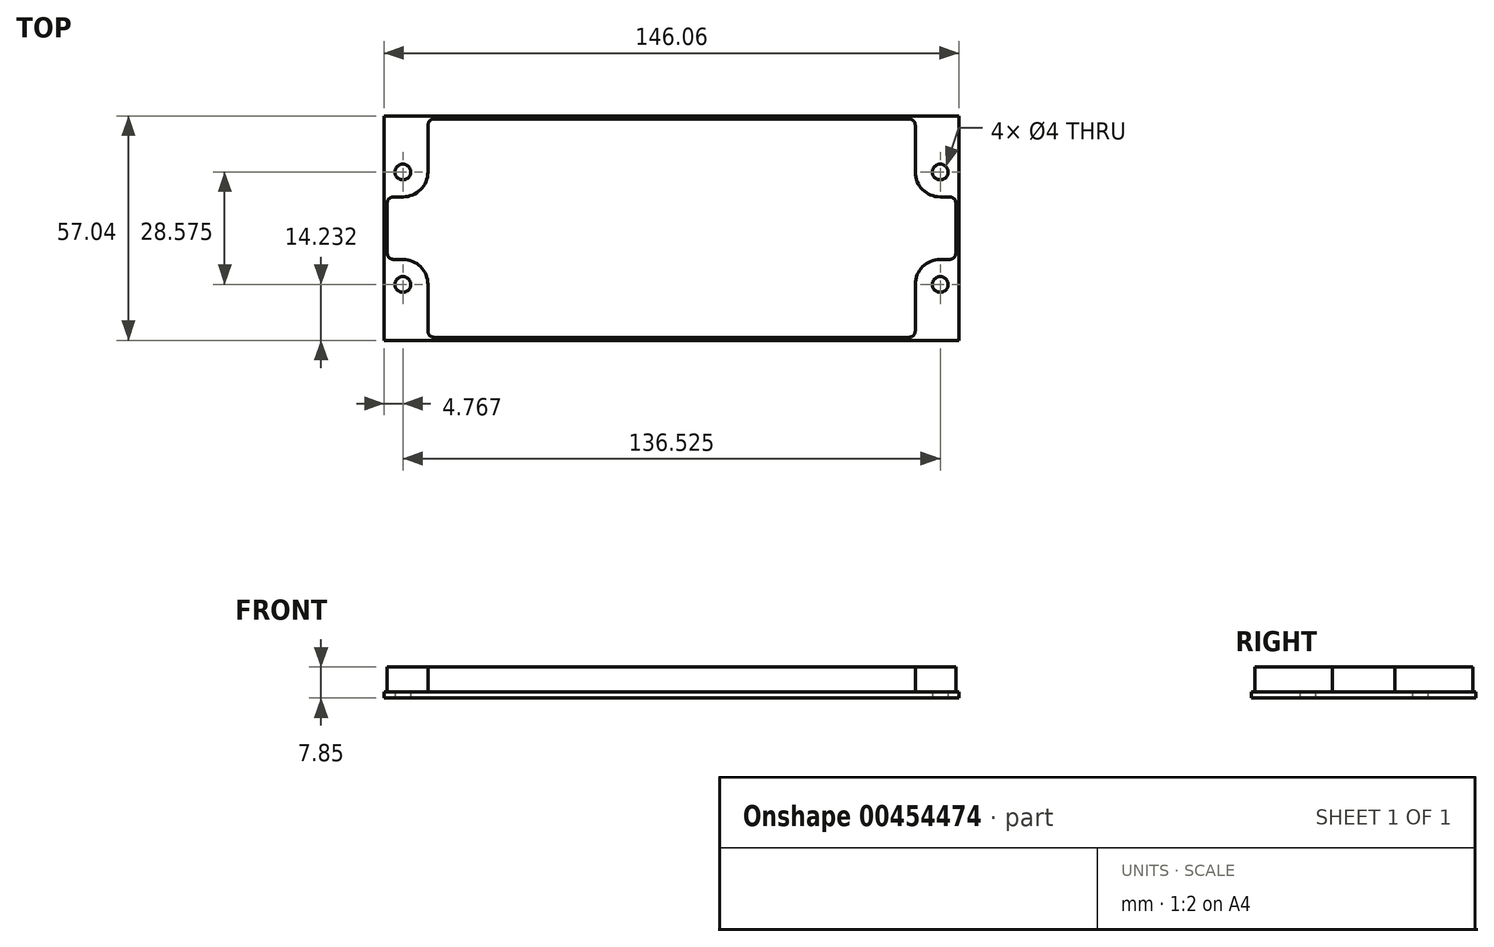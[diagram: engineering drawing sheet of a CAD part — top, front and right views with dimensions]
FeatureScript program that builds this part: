
annotation { "Feature Type Name" : "Feature", "Feature Type Description" : "" }
export const myFeature = defineFeature(function(context is Context, id is Id, definition is map)
    precondition{}
    {
        {
            var Q0;
            Q0=qCreatedBy(makeId("Top.planeOp"),FACE);
            var sketch = newSketch(context, id + "F0", { "sketchPlane" : qUnion([Q0])});
            skLineSegment(sketch, "E0.bottom", {"start": v(-73.03, 28.52) * mm, "end": v(73.03, 28.53) * mm, "construction": true});
            skLineSegment(sketch, "E0.top", {"start": v(-73.03, -28.53) * mm, "end": v(73.03, -28.52) * mm, "construction": true});
            skLineSegment(sketch, "E0.left", {"start": v(-73.03, 28.52) * mm, "end": v(-73.03, -28.53) * mm, "construction": true});
            skLineSegment(sketch, "E0.right", {"start": v(73.03, 28.53) * mm, "end": v(73.03, -28.53) * mm, "construction": true});
            skCircle(sketch, "E1", {"center": v(-68.26, -14.29) * mm, "radius": 4.76 * mm});
            skCircle(sketch, "E2", {"center": v(-68.26, 14.29) * mm, "radius": 4.76 * mm});
            skPoint(sketch, "E3.third.point.positionSnap0", {"position": v(73.03, 0) * mm});
            skCircle(sketch, "E4", {"center": v(68.26, 14.29) * mm, "radius": 4.76 * mm});
            skCircle(sketch, "E5", {"center": v(68.26, -14.29) * mm, "radius": 4.76 * mm});
            skPoint(sketch, "E6", {"position": v(0, 28.53) * mm});
            skLineSegment(sketch, "E7.bottom", {"start": v(-73.03, 28.53) * mm, "end": v(73.03, 28.53) * mm});
            skLineSegment(sketch, "E7.top", {"start": v(-73.03, -28.53) * mm, "end": v(73.03, -28.53) * mm});
            skLineSegment(sketch, "E7.left", {"start": v(-73.03, 28.52) * mm, "end": v(-73.03, -28.53) * mm});
            skLineSegment(sketch, "E7.right", {"start": v(73.03, 28.53) * mm, "end": v(73.03, -28.53) * mm});
            skCircle(sketch, "E8", {"center": v(-68.26, 14.29) * mm, "radius": 2 * mm});
            skCircle(sketch, "E9", {"center": v(68.26, -14.29) * mm, "radius": 2 * mm});
            skCircle(sketch, "E10", {"center": v(-68.26, -14.29) * mm, "radius": 2 * mm});
            skCircle(sketch, "E11", {"center": v(68.26, 14.29) * mm, "radius": 2 * mm});
            skArc(sketch, "E12", {"start": v(68.26, 20.64) * mm, "mid": v(61.91, 14.29) * mm, "end": v(68.26, 7.94) * mm});
            skArc(sketch, "E13", {"start": v(68.26, -7.94) * mm, "mid": v(61.91, -14.29) * mm, "end": v(68.26, -20.64) * mm});
            skArc(sketch, "E14", {"start": v(-68.26, -20.64) * mm, "mid": v(-61.91, -14.29) * mm, "end": v(-68.26, -7.94) * mm});
            skArc(sketch, "E15", {"start": v(-68.26, 7.94) * mm, "mid": v(-61.91, 14.29) * mm, "end": v(-68.26, 20.64) * mm});
            skLineSegment(sketch, "E16", {"start": v(68.26, 20.64) * mm, "end": v(73.03, 20.64) * mm});
            skLineSegment(sketch, "E17", {"start": v(68.26, 7.94) * mm, "end": v(73.03, 7.94) * mm});
            skLineSegment(sketch, "E18", {"start": v(68.26, -7.94) * mm, "end": v(73.03, -7.94) * mm});
            skLineSegment(sketch, "E19", {"start": v(68.26, -20.64) * mm, "end": v(73.03, -20.64) * mm});
            skLineSegment(sketch, "E20", {"start": v(-68.26, -7.94) * mm, "end": v(-73.03, -7.94) * mm});
            skLineSegment(sketch, "E21", {"start": v(-68.26, -20.64) * mm, "end": v(-73.03, -20.64) * mm});
            skLineSegment(sketch, "E22", {"start": v(-68.26, 20.64) * mm, "end": v(-73.03, 20.64) * mm});
            skLineSegment(sketch, "E23", {"start": v(-68.26, 7.94) * mm, "end": v(-73.03, 7.94) * mm});
            skSolve(sketch);
        }
        {
            var Q0;
            {var subQ3=sQuery(id+"F0.wireOp",EDGE,"E7.bottom");Q0=makeQuery(id+"F0.imprint","IMPRINT",FACE,{"disambiguationData":[TD([[makeQuery(id+"F0.imprint","IMPRINT",EDGE,{"derivedFrom":subQ3}),-1.0]])]});}
            var Q1;
            {var subQ2=sQuery(id+"F0.wireOp",EDGE,"E2");Q1=makeQuery(id+"F0.imprint","IMPRINT",FACE,{"disambiguationData":[TD([[makeQuery(id+"F0.imprint","IMPRINT",EDGE,{"derivedFrom":subQ2}),-1.0]])]});}
            var Q2;
            Q2=makeQuery(id+"F0.imprint","IMPRINT",FACE,{"disambiguationData":[TD([[makeQuery(id+"F0.imprint","IMPRINT",EDGE,{"derivedFrom":sQuery(id+"F0.wireOp",EDGE,"E2")}),1.0]])]});
            var Q3;
            {var subQ2=sQuery(id+"F0.wireOp",EDGE,"E1");Q3=makeQuery(id+"F0.imprint","IMPRINT",FACE,{"disambiguationData":[TD([[makeQuery(id+"F0.imprint","IMPRINT",EDGE,{"derivedFrom":subQ2}),-1.0]])]});}
            var Q4;
            Q4=makeQuery(id+"F0.imprint","IMPRINT",FACE,{"disambiguationData":[TD([[makeQuery(id+"F0.imprint","IMPRINT",EDGE,{"derivedFrom":sQuery(id+"F0.wireOp",EDGE,"E1")}),1.0]])]});
            var Q5;
            {var subQ2=sQuery(id+"F0.wireOp",EDGE,"E4");Q5=makeQuery(id+"F0.imprint","IMPRINT",FACE,{"disambiguationData":[TD([[makeQuery(id+"F0.imprint","IMPRINT",EDGE,{"derivedFrom":subQ2}),-1.0]])]});}
            var Q6;
            Q6=makeQuery(id+"F0.imprint","IMPRINT",FACE,{"disambiguationData":[TD([[makeQuery(id+"F0.imprint","IMPRINT",EDGE,{"derivedFrom":sQuery(id+"F0.wireOp",EDGE,"E4")}),1.0]])]});
            var Q7;
            {var subQ0=sQuery(id+"F0.wireOp",EDGE,"E5");Q7=makeQuery(id+"F0.imprint","IMPRINT",FACE,{"disambiguationData":[TD([[makeQuery(id+"F0.imprint","IMPRINT",EDGE,{"derivedFrom":subQ0}),-1.0]])]});}
            var Q8;
            Q8=makeQuery(id+"F0.imprint","IMPRINT",FACE,{"disambiguationData":[TD([[makeQuery(id+"F0.imprint","IMPRINT",EDGE,{"derivedFrom":sQuery(id+"F0.wireOp",EDGE,"E5")}),1.0]])]});
            extrude(context, id + "F1", {"entities" : qUnion([Q0, Q1, Q2, Q3, Q4, Q5, Q6, Q7, Q8]), "depth" : 1.5 * mm});
        }
        {
            var Q0;
            Q0=makeQuery(id+"F1.opExtrude","CAP_FACE",FACE,{"disambiguationData":[OSD([sQuery(id+"F0.wireOp",EDGE,"E7.bottom"),sQuery(id+"F0.wireOp",EDGE,"E7.top"),sQuery(id+"F0.wireOp",EDGE,"E7.left"),sQuery(id+"F0.wireOp",EDGE,"E7.right"),sQuery(id+"F0.wireOp",EDGE,"E8"),sQuery(id+"F0.wireOp",EDGE,"E9"),sQuery(id+"F0.wireOp",EDGE,"E10"),sQuery(id+"F0.wireOp",EDGE,"E11")])],"isStart":false});
            var sketch = newSketch(context, id + "F2", { "sketchPlane" : qUnion([Q0])});
            skLineSegment(sketch, "E24.0", {"start": v(68.26, 7.94) * mm, "end": v(70.64, 7.94) * mm});
            skArc(sketch, "E24.1", {"start": v(68.26, 20.64) * mm, "mid": v(61.91, 14.29) * mm, "end": v(68.26, 7.94) * mm});
            skLineSegment(sketch, "E24.2", {"start": v(68.26, 20.64) * mm, "end": v(70.64, 20.64) * mm});
            skLineSegment(sketch, "E25.0", {"start": v(73.03, 28.53) * mm, "end": v(73.03, -28.53) * mm});
            skLineSegment(sketch, "E25.1", {"start": v(68.26, -7.94) * mm, "end": v(70.64, -7.94) * mm});
            skArc(sketch, "E25.2", {"start": v(68.26, -7.94) * mm, "mid": v(61.91, -14.29) * mm, "end": v(68.26, -20.64) * mm});
            skLineSegment(sketch, "E25.3", {"start": v(68.26, -20.64) * mm, "end": v(70.64, -20.64) * mm});
            skLineSegment(sketch, "E25.4", {"start": v(-73.03, -28.53) * mm, "end": v(73.03, -28.53) * mm});
            skLineSegment(sketch, "E25.5", {"start": v(-73.03, 28.52) * mm, "end": v(-73.03, -28.53) * mm});
            skLineSegment(sketch, "E25.6", {"start": v(-68.26, -20.64) * mm, "end": v(-70.64, -20.64) * mm});
            skArc(sketch, "E25.7", {"start": v(-68.26, -20.64) * mm, "mid": v(-61.91, -14.29) * mm, "end": v(-68.26, -7.94) * mm});
            skLineSegment(sketch, "E25.8", {"start": v(-68.26, -7.94) * mm, "end": v(-70.64, -7.94) * mm});
            skLineSegment(sketch, "E25.9", {"start": v(-73.03, 28.53) * mm, "end": v(73.03, 28.53) * mm});
            skArc(sketch, "E25.10", {"start": v(-68.26, 7.94) * mm, "mid": v(-61.91, 14.29) * mm, "end": v(-68.26, 20.64) * mm});
            skLineSegment(sketch, "E25.11", {"start": v(-68.26, 7.94) * mm, "end": v(-70.64, 7.94) * mm});
            skLineSegment(sketch, "E25.12", {"start": v(-68.26, 20.64) * mm, "end": v(-70.64, 20.64) * mm});
            skLineSegment(sketch, "E26.0", {"start": v(-60.32, 27.73) * mm, "end": v(60.32, 27.73) * mm});
            skLineSegment(sketch, "E26.1", {"start": v(-72.22, 26.14) * mm, "end": v(-72.22, 22.23) * mm});
            skLineSegment(sketch, "E26.2", {"start": v(-60.32, -27.73) * mm, "end": v(60.32, -27.73) * mm});
            skLineSegment(sketch, "E26.3", {"start": v(72.23, 26.14) * mm, "end": v(72.23, 22.23) * mm});
            skPoint(sketch, "E27", {"position": v(-72.23, 7.94) * mm});
            skPoint(sketch, "E28", {"position": v(-72.23, 20.64) * mm});
            skPoint(sketch, "E29", {"position": v(-72.23, -7.94) * mm});
            skPoint(sketch, "E30", {"position": v(-72.23, -20.64) * mm});
            skPoint(sketch, "E31", {"position": v(72.23, -20.64) * mm});
            skPoint(sketch, "E32", {"position": v(72.23, -7.94) * mm});
            skPoint(sketch, "E33", {"position": v(72.23, 20.64) * mm});
            skPoint(sketch, "E34", {"position": v(72.23, 7.94) * mm});
            skLineSegment(sketch, "E35.trimOffspring", {"start": v(72.23, 6.35) * mm, "end": v(72.23, -6.35) * mm});
            skPoint(sketch, "E36.orphan", {"position": v(73.03, 20.64) * mm});
            skPoint(sketch, "E37.orphan", {"position": v(73.03, 7.94) * mm});
            skLineSegment(sketch, "E38.trimOffspring", {"start": v(72.23, -22.23) * mm, "end": v(72.23, -26.14) * mm});
            skPoint(sketch, "E39.orphan", {"position": v(73.03, -20.64) * mm});
            skPoint(sketch, "E40.orphan", {"position": v(73.03, -7.94) * mm});
            skLineSegment(sketch, "E41.trimOffspring", {"start": v(-72.23, -22.23) * mm, "end": v(-72.23, -26.14) * mm});
            skPoint(sketch, "E42.orphan", {"position": v(-73.03, -20.64) * mm});
            skPoint(sketch, "E43.orphan", {"position": v(-73.03, -7.94) * mm});
            skPoint(sketch, "E44.orphan", {"position": v(-73.03, 20.64) * mm});
            skLineSegment(sketch, "E45.trimOffspring", {"start": v(-72.23, 6.35) * mm, "end": v(-72.23, -6.35) * mm});
            skPoint(sketch, "E46.orphan", {"position": v(-73.03, 7.94) * mm});
            skArc(sketch, "E47.filletArc", {"start": v(-72.23, 22.23) * mm, "mid": v(-71.76, 21.1) * mm, "end": v(-70.64, 20.64) * mm});
            skArc(sketch, "E48.filletArc", {"start": v(-70.64, 7.94) * mm, "mid": v(-71.76, 7.47) * mm, "end": v(-72.23, 6.35) * mm});
            skPoint(sketch, "E49.visualSharp", {"position": v(-72.23, 27.73) * mm});
            skArc(sketch, "E49.filletArc", {"start": v(-70.64, 27.73) * mm, "mid": v(-71.76, 27.26) * mm, "end": v(-72.23, 26.14) * mm});
            skArc(sketch, "E50.filletArc", {"start": v(-72.23, -6.35) * mm, "mid": v(-71.76, -7.47) * mm, "end": v(-70.64, -7.94) * mm});
            skArc(sketch, "E51.filletArc", {"start": v(-70.64, -20.64) * mm, "mid": v(-71.76, -21.1) * mm, "end": v(-72.23, -22.23) * mm});
            skPoint(sketch, "E52.visualSharp", {"position": v(-72.23, -27.73) * mm});
            skArc(sketch, "E52.filletArc", {"start": v(-72.23, -26.14) * mm, "mid": v(-71.76, -27.26) * mm, "end": v(-70.64, -27.73) * mm});
            skPoint(sketch, "E53.visualSharp", {"position": v(72.23, -27.73) * mm});
            skArc(sketch, "E53.filletArc", {"start": v(70.64, -27.73) * mm, "mid": v(71.76, -27.26) * mm, "end": v(72.23, -26.14) * mm});
            skArc(sketch, "E54.filletArc", {"start": v(72.23, -22.23) * mm, "mid": v(71.76, -21.1) * mm, "end": v(70.64, -20.64) * mm});
            skArc(sketch, "E55.filletArc", {"start": v(70.64, -7.94) * mm, "mid": v(71.76, -7.47) * mm, "end": v(72.23, -6.35) * mm});
            skArc(sketch, "E56.filletArc", {"start": v(72.23, 6.35) * mm, "mid": v(71.76, 7.47) * mm, "end": v(70.64, 7.94) * mm});
            skArc(sketch, "E57.filletArc", {"start": v(70.64, 20.64) * mm, "mid": v(71.76, 21.1) * mm, "end": v(72.23, 22.23) * mm});
            skPoint(sketch, "E58.visualSharp", {"position": v(72.23, 27.73) * mm});
            skArc(sketch, "E58.filletArc", {"start": v(72.23, 26.14) * mm, "mid": v(71.76, 27.26) * mm, "end": v(70.64, 27.73) * mm});
            skLineSegment(sketch, "E59", {"start": v(61.91, 14.29) * mm, "end": v(61.91, 26.14) * mm});
            skLineSegment(sketch, "E60", {"start": v(61.91, -14.29) * mm, "end": v(61.91, -26.14) * mm});
            skLineSegment(sketch, "E61", {"start": v(-61.91, 14.29) * mm, "end": v(-61.91, 26.14) * mm});
            skLineSegment(sketch, "E62", {"start": v(-61.91, -14.29) * mm, "end": v(-61.91, -26.14) * mm});
            skArc(sketch, "E63.filletArc", {"start": v(-60.32, 27.73) * mm, "mid": v(-61.45, 27.26) * mm, "end": v(-61.91, 26.14) * mm});
            skArc(sketch, "E64.filletArc", {"start": v(61.91, 26.14) * mm, "mid": v(61.45, 27.26) * mm, "end": v(60.32, 27.73) * mm});
            skArc(sketch, "E65.filletArc", {"start": v(60.32, -27.73) * mm, "mid": v(61.45, -27.26) * mm, "end": v(61.91, -26.14) * mm});
            skArc(sketch, "E66.filletArc", {"start": v(-61.91, -26.14) * mm, "mid": v(-61.45, -27.26) * mm, "end": v(-60.32, -27.73) * mm});
            skSolve(sketch);
        }
        {
            var Q0;
            Q0=makeQuery(id+"F2.imprint","IMPRINT",FACE,{"disambiguationData":[TD([[makeQuery(id+"F2.imprint","IMPRINT",EDGE,{"derivedFrom":sQuery(id+"F2.wireOp",EDGE,"E24.0")}),-1.0]])]});
            extrude(context, id + "F3", {"entities" : qUnion([Q0]), "depth" : 6.35 * mm});
        }
    });
